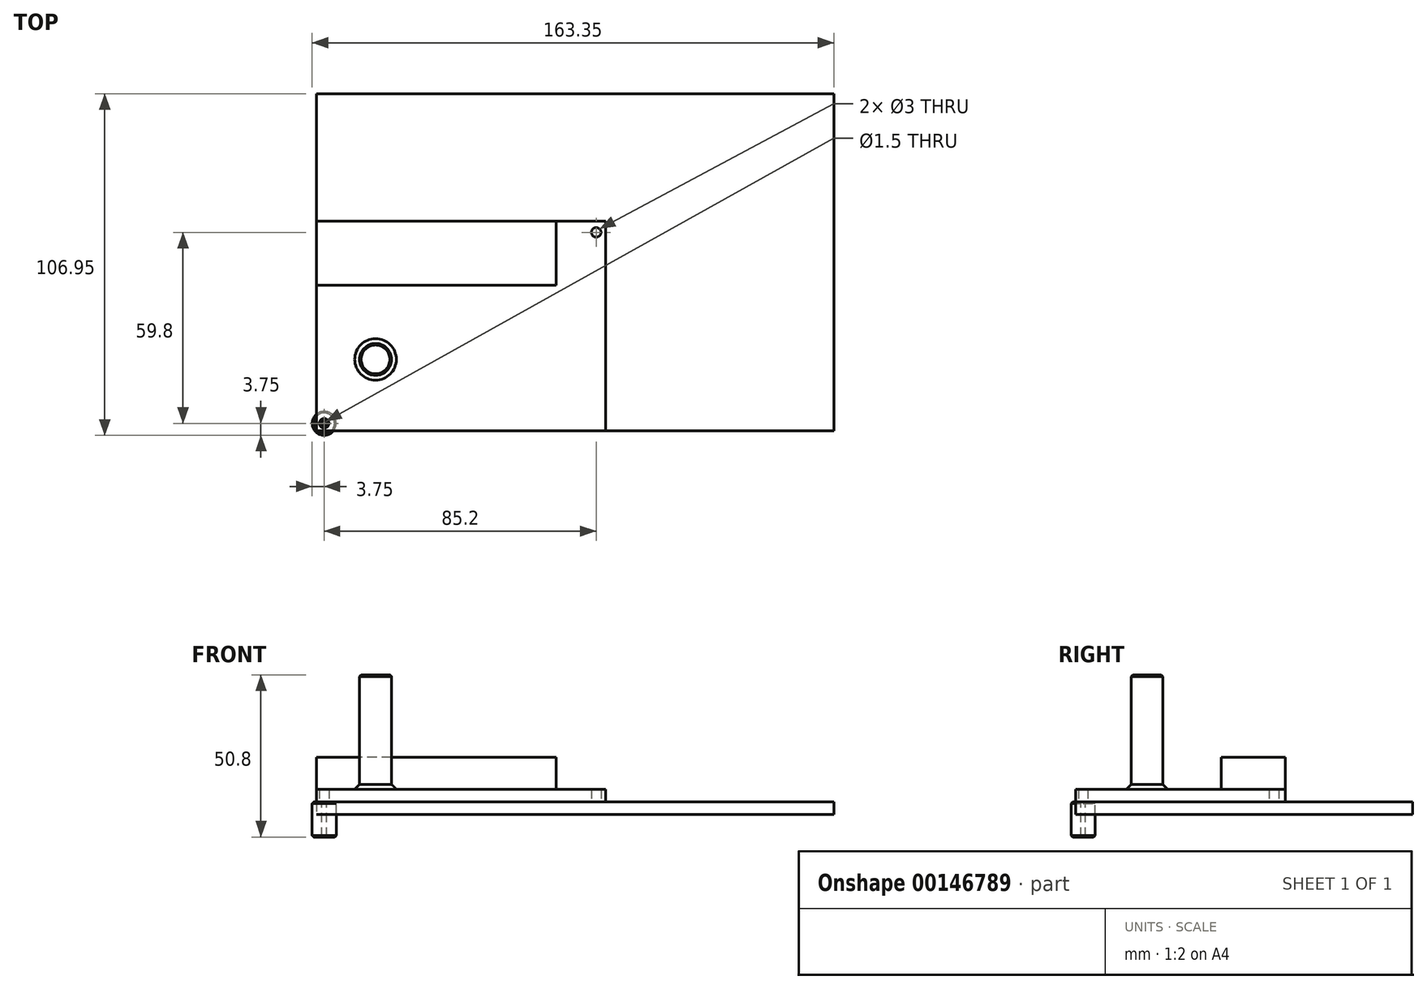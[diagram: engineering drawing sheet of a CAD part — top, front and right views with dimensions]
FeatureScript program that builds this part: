
annotation { "Feature Type Name" : "Feature", "Feature Type Description" : "" }
export const myFeature = defineFeature(function(context is Context, id is Id, definition is map)
    precondition{}
    {
        {
            var Q0;
            Q0=qCreatedBy(makeId("Top.planeOp"),FACE);
            var sketch = newSketch(context, id + "F0", { "sketchPlane" : qUnion([Q0])});
            skLineSegment(sketch, "E0.bottom", {"start": v(81, -52.75) * mm, "end": v(-81, -52.75) * mm});
            skLineSegment(sketch, "E0.top", {"start": v(81, 52.75) * mm, "end": v(-81, 52.75) * mm});
            skLineSegment(sketch, "E0.left", {"start": v(81, -52.75) * mm, "end": v(81, 52.75) * mm});
            skLineSegment(sketch, "E0.right", {"start": v(-81, -52.75) * mm, "end": v(-81, 52.75) * mm});
            skPoint(sketch, "E0.middle", {"position": v(0, 0) * mm});
            skSolve(sketch);
        }
        {
            var Q0;
            Q0 = qSketchRegion(id + "F0", true);
            extrude(context, id + "F1", {"entities" : qUnion([Q0]), "depth" : 4 * mm});
        }
        {
            var Q0;
            Q0=makeQuery(id+"F1.opExtrude","CAP_FACE",FACE,{"disambiguationData":[OSD([sQuery(id+"F0.wireOp",EDGE,"E0.bottom"),sQuery(id+"F0.wireOp",EDGE,"E0.top"),sQuery(id+"F0.wireOp",EDGE,"E0.left"),sQuery(id+"F0.wireOp",EDGE,"E0.right")])],"isStart":false});
            var sketch = newSketch(context, id + "F2", { "sketchPlane" : qUnion([Q0])});
            skLineSegment(sketch, "E1.bottom", {"start": v(-81, -52.75) * mm, "end": v(9.6, -52.75) * mm});
            skLineSegment(sketch, "E1.top", {"start": v(-81, 12.85) * mm, "end": v(9.6, 12.85) * mm});
            skLineSegment(sketch, "E1.left", {"start": v(-81, -52.75) * mm, "end": v(-81, 12.85) * mm});
            skLineSegment(sketch, "E1.right", {"start": v(9.6, -52.75) * mm, "end": v(9.6, 12.85) * mm});
            skCircle(sketch, "E2", {"center": v(6.6, 9.35) * mm, "radius": 1.5 * mm});
            skCircle(sketch, "E3", {"center": v(-78.6, -50.45) * mm, "radius": 1.5 * mm});
            skSolve(sketch);
        }
        {
            var Q0;
            Q0 = qSketchRegion(id + "F2", true);
            extrude(context, id + "F3", {"entities" : qUnion([Q0]), "depth" : 4 * mm});
        }
        {
            var Q0;
            Q0=makeQuery(id+"F3.opExtrude","CAP_FACE",FACE,{"disambiguationData":[OSD([sQuery(id+"F2.wireOp",EDGE,"E1.bottom"),sQuery(id+"F2.wireOp",EDGE,"E1.top"),sQuery(id+"F2.wireOp",EDGE,"E1.left"),sQuery(id+"F2.wireOp",EDGE,"E1.right"),sQuery(id+"F2.wireOp",EDGE,"E2"),sQuery(id+"F2.wireOp",EDGE,"E3")])],"isStart":false});
            var sketch = newSketch(context, id + "F4", { "sketchPlane" : qUnion([Q0])});
            skLineSegment(sketch, "E4.bottom", {"start": v(-6, 12.85) * mm, "end": v(-81, 12.85) * mm});
            skLineSegment(sketch, "E4.top", {"start": v(-6, -7.15) * mm, "end": v(-81, -7.15) * mm});
            skLineSegment(sketch, "E4.left", {"start": v(-6, 12.85) * mm, "end": v(-6, -7.15) * mm});
            skLineSegment(sketch, "E4.right", {"start": v(-81, 12.85) * mm, "end": v(-81, -7.15) * mm});
            skSolve(sketch);
        }
        {
            var Q0;
            Q0 = qSketchRegion(id + "F4", true);
            extrude(context, id + "F5", {"entities" : qUnion([Q0]), "operationType" : NewBodyOperationType.ADD, "depth" : 10 * mm});
        }
        {
            var Q0;
            Q0=makeQuery(id+"F3.opExtrude","CAP_FACE",FACE,{"disambiguationData":[OSD([sQuery(id+"F2.wireOp",EDGE,"E1.bottom"),sQuery(id+"F2.wireOp",EDGE,"E1.top"),sQuery(id+"F2.wireOp",EDGE,"E1.left"),sQuery(id+"F2.wireOp",EDGE,"E1.right"),sQuery(id+"F2.wireOp",EDGE,"E2"),sQuery(id+"F2.wireOp",EDGE,"E3")])],"isStart":false});
            var sketch = newSketch(context, id + "F6", { "sketchPlane" : qUnion([Q0])});
            skCircle(sketch, "E5", {"center": v(-62.52, -30.43) * mm, "radius": 5 * mm});
            skSolve(sketch);
        }
        {
            var Q0;
            Q0=makeQuery(id+"F6.imprint","IMPRINT",FACE,{"disambiguationData":[TD([[makeQuery(id+"F6.imprint","IMPRINT",EDGE,{"derivedFrom":sQuery(id+"F6.wireOp",EDGE,"E5")}),1.0]])]});
            extrude(context, id + "F7", {"entities" : qUnion([Q0]), "depth" : 35.8 * mm});
        }
        {
            var Q0;
            Q0=makeQuery(id+"F7.opExtrude","CAP_FACE",FACE,{"disambiguationData":[OSD([sQuery(id+"F6.wireOp",EDGE,"E5")])],"isStart":true});
            var sketch = newSketch(context, id + "F8", { "sketchPlane" : qUnion([Q0])});
            skCircle(sketch, "E6", {"center": v(-62.52, 30.43) * mm, "radius": 6.5 * mm});
            skSolve(sketch);
        }
        {
            var Q0;
            Q0=makeQuery(id+"F8.imprint","IMPRINT",FACE,{"disambiguationData":[TD([[makeQuery(id+"F8.imprint","IMPRINT",EDGE,{"derivedFrom":sQuery(id+"F8.wireOp",EDGE,"E6")}),1.0]])]});
            var Q1;
            Q1=makeQuery(id+"F8.imprint","IMPRINT",FACE,{"disambiguationData":[TD([[makeQuery(id+"F8.imprint","IMPRINT",EDGE,{"derivedFrom":makeQuery(id+"F7.opExtrude","CAP_EDGE",EDGE,{"disambiguationData":[OSD([sQuery(id+"F6.wireOp",EDGE,"E5")])],"isStart":true})}),-1.0]])]});
            extrude(context, id + "F9", {"entities" : qUnion([Q0, Q1]), "operationType" : NewBodyOperationType.ADD, "oppositeDirection" : true, "depth" : 2 * mm, "hasDraft" : true, "draftAngle" : 45 * degree, "draftPullDirection" : true});
        }
        {
            var Q0;
            Q0=makeQuery(id+"F7.opExtrude","CAP_EDGE",EDGE,{"disambiguationData":[OSD([sQuery(id+"F6.wireOp",EDGE,"E5")])],"isStart":false});
            chamfer(context, id + "F10", {"entities" : qUnion([Q0]), "width" : 0.5 * mm, "tangentPropagation" : true});
        }
        {
            var Q0;
            Q0=makeQuery(id+"F3.opExtrude","CAP_FACE",FACE,{"disambiguationData":[OSD([sQuery(id+"F2.wireOp",EDGE,"E1.bottom"),sQuery(id+"F2.wireOp",EDGE,"E1.top"),sQuery(id+"F2.wireOp",EDGE,"E1.left"),sQuery(id+"F2.wireOp",EDGE,"E1.right"),sQuery(id+"F2.wireOp",EDGE,"E2"),sQuery(id+"F2.wireOp",EDGE,"E3")])],"isStart":true});
            var sketch = newSketch(context, id + "F11", { "sketchPlane" : qUnion([Q0])});
            skCircle(sketch, "E7", {"center": v(6.6, -9.35) * mm, "radius": 3.75 * mm});
            skCircle(sketch, "E8", {"center": v(-78.6, 50.45) * mm, "radius": 3.75 * mm});
            skCircle(sketch, "E9", {"center": v(-78.6, 50.45) * mm, "radius": 0.75 * mm});
            skCircle(sketch, "E10", {"center": v(6.6, -9.35) * mm, "radius": 0.75 * mm});
            skSolve(sketch);
        }
        {
            var Q0;
            Q0 = qSketchRegion(id + "F11", true);
            extrude(context, id + "F12", {"entities" : qUnion([Q0]), "depth" : 11 * mm});
        }
        {
            var Q0;
            Q0=makeQuery(id+"F12.opExtrude","SWEPT_BODY",BODY,{"disambiguationData":[OSD([sQuery(id+"F11.wireOp",EDGE,"E7"),sQuery(id+"F11.wireOp",EDGE,"E10")])]});
            deleteBodies(context, id + "F13", {"entities" : qUnion([Q0])});
        }
        {
            var Q0;
            Q0=makeQuery(id+"F12.opExtrude","SWEPT_FACE",FACE,{"disambiguationData":[OSD([sQuery(id+"F11.wireOp",EDGE,"E8")])]});
            chamfer(context, id + "F14", {"entities" : qUnion([Q0]), "width" : 0.5 * mm, "tangentPropagation" : true});
        }
    });
